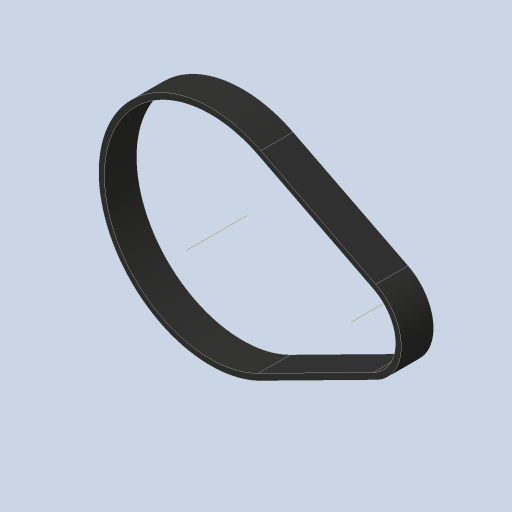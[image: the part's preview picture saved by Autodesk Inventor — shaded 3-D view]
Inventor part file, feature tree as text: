
AUTODESK INVENTOR PART (.ipt)
format: ipt  version: 2023.4 (Build 274418000, 418)  size: 169,984 bytes
history: native  units: in
note: dims shown in document units (in); Inventor stores cm internally (conversion verified against a paired STEP export)
features: sketch x3, extrude x1, other x1, projected_geometry x1
ambient origin geometry x8: Origin, YZ Plane, XZ Plane, XY Plane, X Axis, Y Axis, Z Axis, Center Point
bodies: Body1 (feature_tree)
feature tree (6):
  sketch  "Sketch2"  dims[d0=0.9023in d1=2.2558in]
  extrude  "Extrusion2"  Depth=2.2558in
  sketch  "Sketch5"  dims[d3=4.6009in d5=1.3362in d9=0.0787in d10=0.0598in d11=0.0299in d12=0.0219in d13=0.0219in d14=0.0059in d15=0.0059in d20=0.3346in d21=0.0in d22=0.0787in d23=0.0598in d24=0.0299in d25=0.0219in d26=0.0219in d27=0.0059in d28=0.0059in d29=0.0299in d30=0.0394in d31=0.0787in d32=0.0232in d34=0.0219in d35=0.0in d36=0.0in d37=0.0059in d38=0.0022in d39=0.0022in d40=0.0in d41=0.0in d42=0.0081in d43=0.0081in d44=0.0299in]
  other  "Work Axis1"
  sketch  "Sketch4"  dims[d2=0.9944in]
  projected_geometry  "Projected Loop1"
